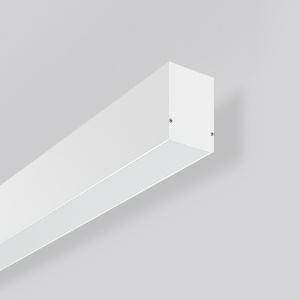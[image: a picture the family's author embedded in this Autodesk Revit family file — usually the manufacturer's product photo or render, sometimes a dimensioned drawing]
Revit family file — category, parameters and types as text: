
# Revit family: less_is_more_50_312611_002_c38e
name_source: partatom
category: Lighting Fixtures
units: mm (PartAtom-declared; Revit-internal decimal feet)

## family parameters
Cut with Voids When Loaded = No
Host = Face
Light Source = No
Part Type = Normal
Room Calculation Point = No
Round Connector Dimension = Use Diameter
Shared = No

## types (1)
- LESS IS MORE 50 (1 x LED Modul 830, 2200 lm, 3000)
    Apparent Load = 18 VA
    CIE Flux Codes = 48 80 96 100 100
    Color Rendering = 80
    Color Temperature = 3000
    Default Elevation = 1800 mm
    Description = Series: LESS IS MORE 50
Linear wall luminaires. Housing: extruded aluminium profile, powder-coated. End cap aluminium powder-coated. Diffuser made of non-yellowing plastic (PMMA), opal. Direct light emission. Suitable for Wall (surface). LED unit with integrated converter interchangeable and removable. Suitable for through-wiring. With sensors or as a safety luminaire on request. 
Colour: traffic white, matt (RAL 9016)
Length: 1687 mm
Width: 67 mm
Height: 75 mm
Lamp: LED
Socket: without socket
Colour temperature: 3000K
Colour rendering index (CRI): 80
System power: 18 W
Rated luminous flux: 2200 lm
Luminous efficiency: 122 lm/W
Control gear: Regulated power supply
Protection class: I
Type of protection: IP 20
    Height = 75 mm
    Lamp = 1 x LED Modul 830
    Lamp Light Flux = 2200 lm
    Lamp count = 1
    Length = 1687 mm
    Lifetime = 50000 h
    Luminous efficacy = 122 lm/W
    Manufacturer = RZB
    ModVariant = No
    Model = 312611.002
    Mounting Place = Wall
    Mounting Type = Surface mounted
    Number of Poles = 1
    OnlyDefault = Yes
    Power Factor = 1
    Product Name = LESS IS MORE 50
    Product group = Surface mounted LED linear luminaires
    ProductGroupID = 2007
    Protection Class = Protection class I
    Protection Degree = IP 20
    RLX_Detail_Level = 1
    RLX_Emergency_Light_Flux = 0 lm
    RLX_Emergency_Type = 0
    RLX_Emergency_Type_DB = No
    RlxData = <blob elided: 35189 chars, md5=2767324b>
    Socket = socket
    Standby Power = 0 W
    System Light Flux = 2200 lm
    System Power = 18 W
    Type Comments = Product without accessories
    Type Image = 312606.002.jpg
    URL = http://relux.com
    VarID = ---
    Voltage = 0 V
    Weight = 0.00 kg
    Width = 67 mm

## geometry (parser evidence)
native form markers: Blend x4, Sweep x9
no freeform markers — native parametric forms only
